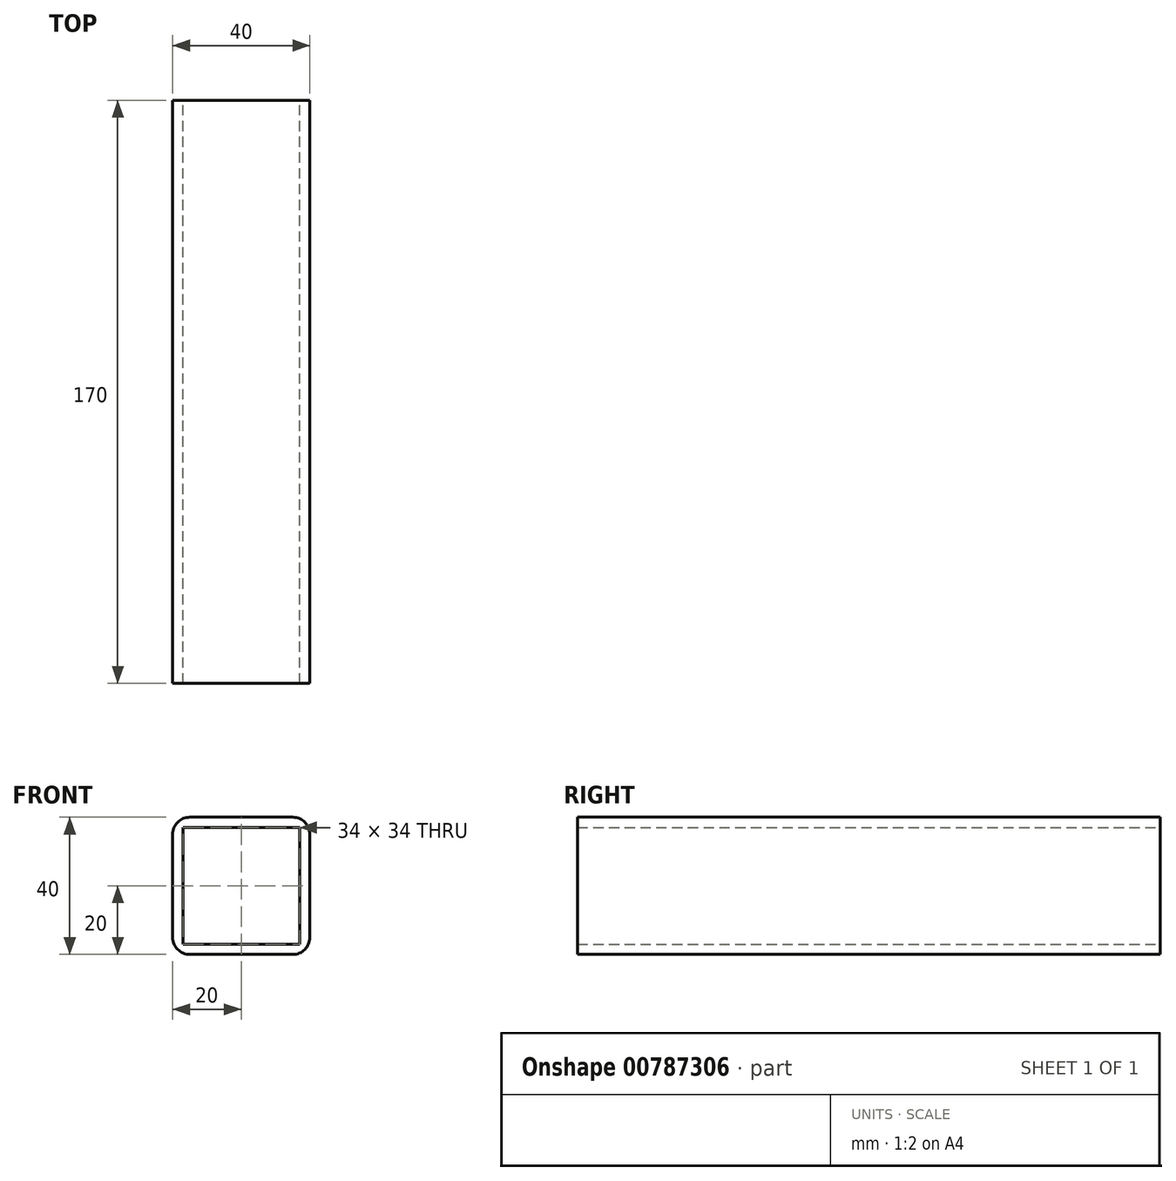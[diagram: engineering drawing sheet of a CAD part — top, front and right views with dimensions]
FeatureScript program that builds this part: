
annotation { "Feature Type Name" : "Feature", "Feature Type Description" : "" }
export const myFeature = defineFeature(function(context is Context, id is Id, definition is map)
    precondition{}
    {
        {
            var Q0;
            Q0=qCreatedBy(makeId("Front.planeOp"),FACE);
            var sketch = newSketch(context, id + "F0", { "sketchPlane" : qUnion([Q0])});
            skLineSegment(sketch, "E0.bottom", {"start": v(15, 20) * mm, "end": v(-15, 20) * mm});
            skLineSegment(sketch, "E0.top", {"start": v(15, -20) * mm, "end": v(-15, -20) * mm});
            skLineSegment(sketch, "E0.left", {"start": v(20, 15) * mm, "end": v(20, -15) * mm});
            skLineSegment(sketch, "E0.right", {"start": v(-20, 15) * mm, "end": v(-20, -15) * mm});
            skPoint(sketch, "E0.middle", {"position": v(0, 0) * mm});
            skPoint(sketch, "E1.visualSharp", {"position": v(-20, 20) * mm});
            skArc(sketch, "E1.filletArc", {"start": v(-15, 20) * mm, "mid": v(-18.54, 18.54) * mm, "end": v(-20, 15) * mm});
            skPoint(sketch, "E2.visualSharp", {"position": v(20, 20) * mm});
            skArc(sketch, "E2.filletArc", {"start": v(20, 15) * mm, "mid": v(18.54, 18.54) * mm, "end": v(15, 20) * mm});
            skPoint(sketch, "E3.visualSharp", {"position": v(20, -20) * mm});
            skArc(sketch, "E3.filletArc", {"start": v(15, -20) * mm, "mid": v(18.54, -18.54) * mm, "end": v(20, -15) * mm});
            skPoint(sketch, "E4.visualSharp", {"position": v(-20, -20) * mm});
            skArc(sketch, "E4.filletArc", {"start": v(-20, -15) * mm, "mid": v(-18.54, -18.54) * mm, "end": v(-15, -20) * mm});
            skLineSegment(sketch, "E5.0", {"start": v(-17, 17) * mm, "end": v(-17, -17) * mm});
            skLineSegment(sketch, "E5.1", {"start": v(17, 17) * mm, "end": v(-17, 17) * mm});
            skLineSegment(sketch, "E5.2", {"start": v(17, 17) * mm, "end": v(17, -17) * mm});
            skLineSegment(sketch, "E5.3", {"start": v(17, -17) * mm, "end": v(-17, -17) * mm});
            skSolve(sketch);
        }
        {
            var Q0;
            Q0=makeQuery(id+"F0.imprint","IMPRINT",FACE,{"disambiguationData":[TD([[makeQuery(id+"F0.imprint","IMPRINT",EDGE,{"derivedFrom":sQuery(id+"F0.wireOp",EDGE,"E0.bottom")}),1.0]])]});
            extrude(context, id + "F1", {"entities" : qUnion([Q0]), "depth" : 170 * mm, "offsetDistance" : 25 * mm});
        }
    });
